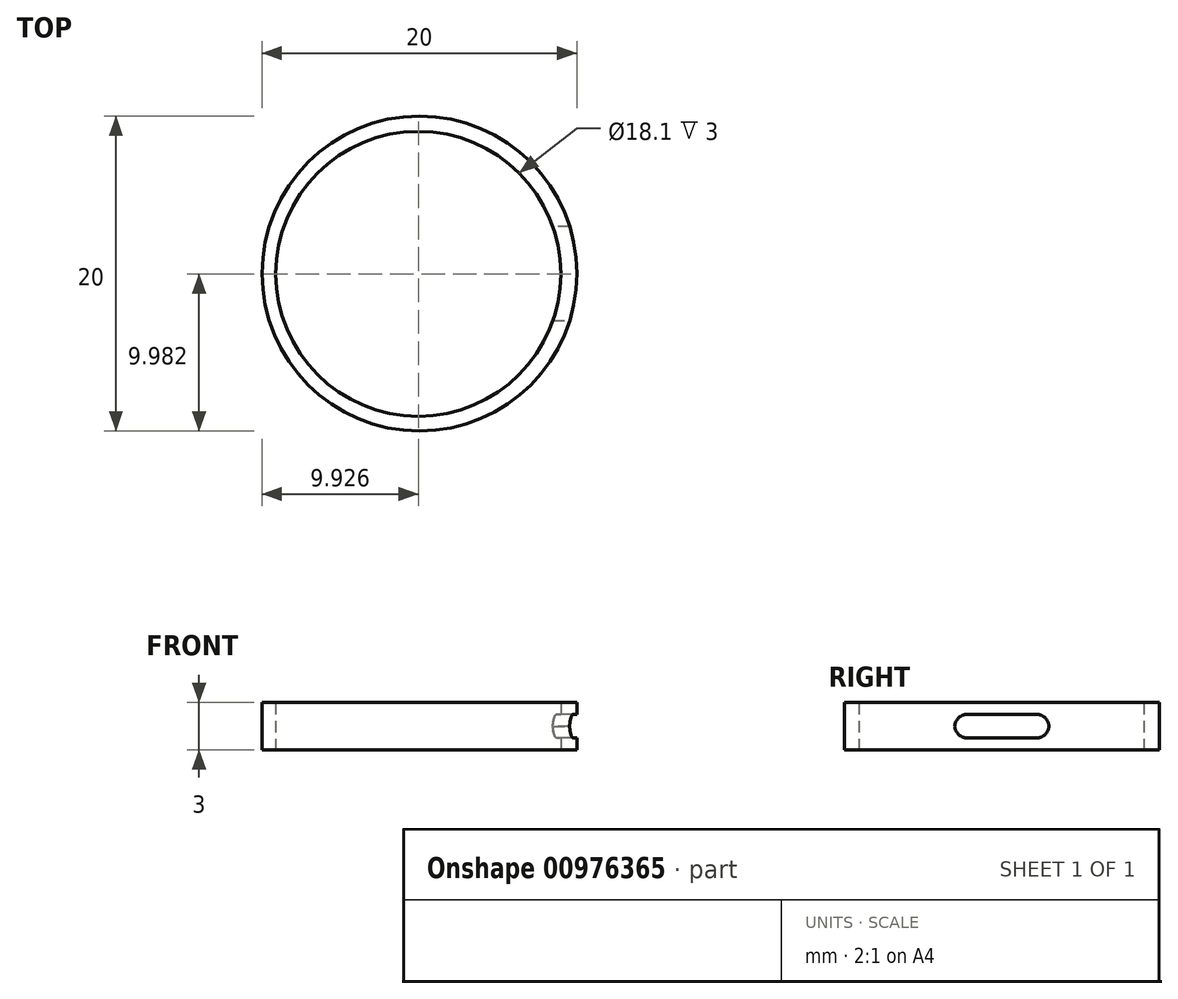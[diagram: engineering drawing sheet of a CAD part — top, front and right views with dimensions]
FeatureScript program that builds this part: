
annotation { "Feature Type Name" : "Feature", "Feature Type Description" : "" }
export const myFeature = defineFeature(function(context is Context, id is Id, definition is map)
    precondition{}
    {
        {
            var Q0;
            Q0=qCreatedBy(makeId("Top.planeOp"),FACE);
            var sketch = newSketch(context, id + "F0", { "sketchPlane" : qUnion([Q0])});
            skCircle(sketch, "E0", {"center": v(0, 0) * mm, "radius": 10 * mm});
            skCircle(sketch, "E1", {"center": v(-0.07, -0.02) * mm, "radius": 9.05 * mm});
            skSolve(sketch);
        }
        {
            var Q0;
            Q0=makeQuery(id+"F0.imprint","IMPRINT",FACE,{"disambiguationData":[TD([[makeQuery(id+"F0.imprint","IMPRINT",EDGE,{"derivedFrom":sQuery(id+"F0.wireOp",EDGE,"E0")}),1.0]])]});
            extrude(context, id + "F1", {"entities" : qUnion([Q0]), "depth" : 3 * mm, "offsetDistance" : 25 * mm});
        }
        {
            var Q0;
            Q0=qCreatedBy(makeId("Right.planeOp"),FACE);
            var sketch = newSketch(context, id + "F2", { "sketchPlane" : qUnion([Q0])});
            skLineSegment(sketch, "E2", {"start": v(0, 0) * mm, "end": v(0, 1.5) * mm});
            skLineSegment(sketch, "E3.bottom", {"start": v(3, 2.25) * mm, "end": v(-3, 2.25) * mm});
            skLineSegment(sketch, "E3.top", {"start": v(3, 0.75) * mm, "end": v(-3, 0.75) * mm});
            skLineSegment(sketch, "E3.left", {"start": v(3, 2.25) * mm, "end": v(3, 0.75) * mm});
            skLineSegment(sketch, "E3.right", {"start": v(-3, 2.25) * mm, "end": v(-3, 0.75) * mm});
            skPoint(sketch, "E3.middle", {"position": v(0, 1.5) * mm});
            skSolve(sketch);
        }
        {
            var Q0;
            Q0=makeQuery(id+"F2.imprint","IMPRINT",FACE,{"disambiguationData":[TD([[makeQuery(id+"F2.imprint","IMPRINT",EDGE,{"derivedFrom":sQuery(id+"F2.wireOp",EDGE,"E3.bottom")}),1.0]])]});
            extrude(context, id + "F3", {"entities" : qUnion([Q0]), "operationType" : NewBodyOperationType.REMOVE, "depth" : 25 * mm, "offsetDistance" : 25 * mm});
        }
        {
            var Q0;
            Q0=makeQuery(id+"F3.boolean.opBoolean","COPY",EDGE,{"derivedFrom":makeQuery(id+"F3.opExtrude","SWEPT_EDGE",EDGE,{"disambiguationData":[OSD([sQuery(id+"F2.wireOp",EDGE,"E3.bottom"),sQuery(id+"F2.wireOp",EDGE,"E3.right")])]})});
            var Q1;
            Q1=makeQuery(id+"F3.boolean.opBoolean","COPY",EDGE,{"derivedFrom":makeQuery(id+"F3.opExtrude","SWEPT_EDGE",EDGE,{"disambiguationData":[OSD([sQuery(id+"F2.wireOp",EDGE,"E3.top"),sQuery(id+"F2.wireOp",EDGE,"E3.right")])]})});
            var Q2;
            Q2=makeQuery(id+"F3.boolean.opBoolean","COPY",EDGE,{"derivedFrom":makeQuery(id+"F3.opExtrude","SWEPT_EDGE",EDGE,{"disambiguationData":[OSD([sQuery(id+"F2.wireOp",EDGE,"E3.bottom"),sQuery(id+"F2.wireOp",EDGE,"E3.left")])]})});
            var Q3;
            Q3=makeQuery(id+"F3.boolean.opBoolean","COPY",EDGE,{"derivedFrom":makeQuery(id+"F3.opExtrude","SWEPT_EDGE",EDGE,{"disambiguationData":[OSD([sQuery(id+"F2.wireOp",EDGE,"E3.top"),sQuery(id+"F2.wireOp",EDGE,"E3.left")])]})});
            fillet(context, id + "F4", {"entities" : qUnion([Q0, Q1, Q2, Q3]), "radius" : .8 * mm, "tangentPropagation" : true, "allowEdgeOverflow" : false});
        }
    });
